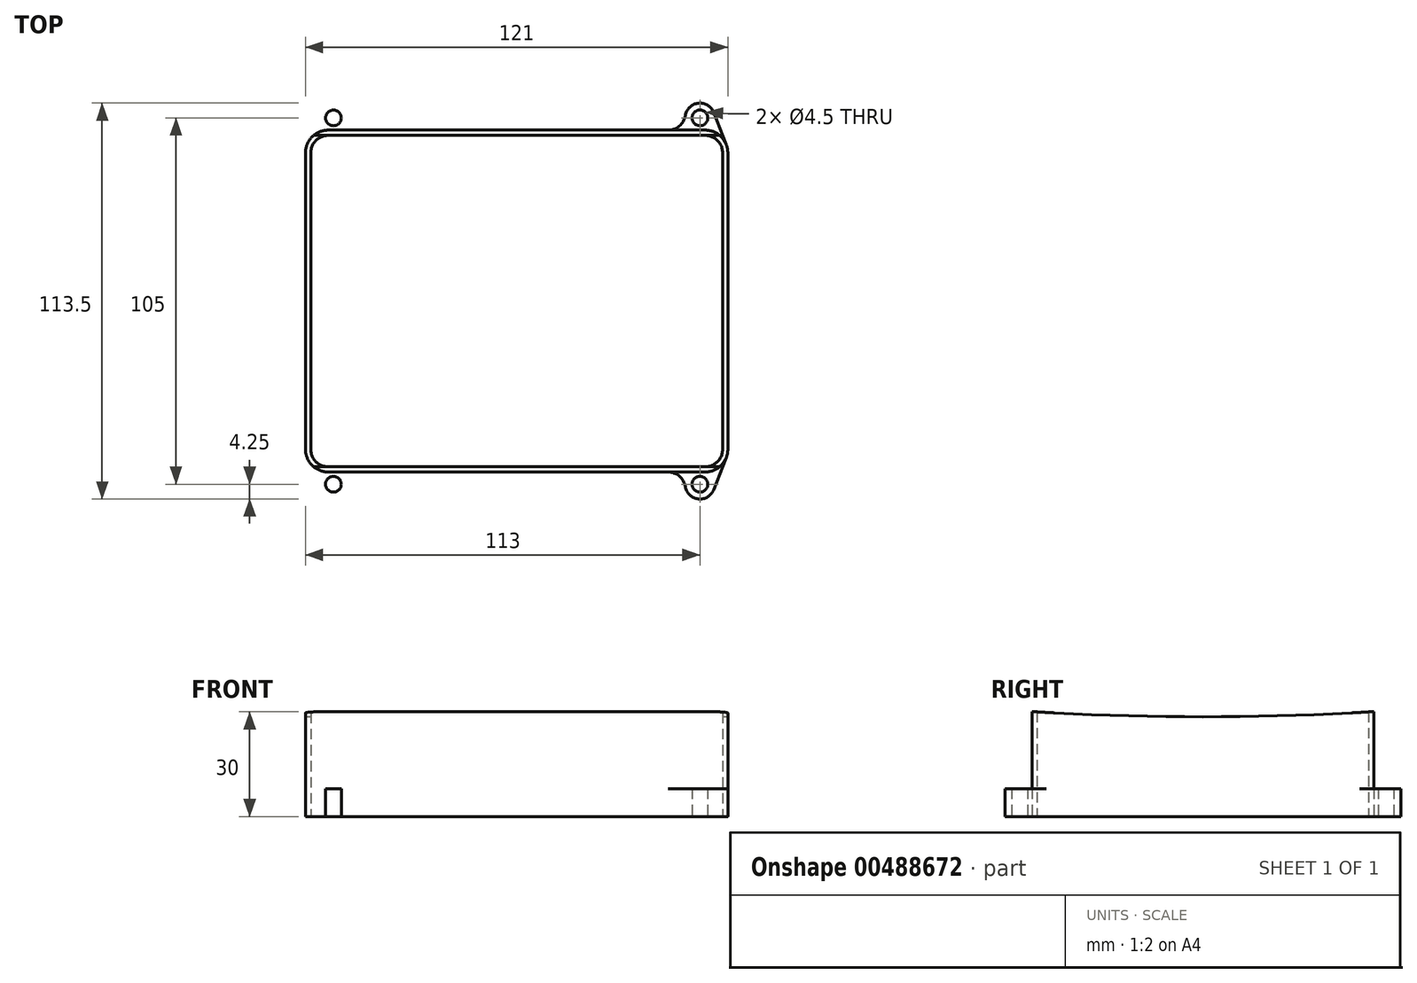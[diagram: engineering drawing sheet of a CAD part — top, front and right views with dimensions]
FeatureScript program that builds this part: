
annotation { "Feature Type Name" : "Feature", "Feature Type Description" : "" }
export const myFeature = defineFeature(function(context is Context, id is Id, definition is map)
    precondition{}
    {
        {
            var Q0;
            Q0=qCreatedBy(makeId("Top.planeOp"),FACE);
            var sketch = newSketch(context, id + "F0", { "sketchPlane" : qUnion([Q0])});
            skLineSegment(sketch, "E0.bottom", {"start": v(54, 47.5) * mm, "end": v(-54, 47.5) * mm});
            skLineSegment(sketch, "E0.top", {"start": v(54, -47.5) * mm, "end": v(-54, -47.5) * mm});
            skLineSegment(sketch, "E0.left", {"start": v(59, 42.5) * mm, "end": v(59, -42.5) * mm});
            skLineSegment(sketch, "E0.right", {"start": v(-59, 42.5) * mm, "end": v(-59, -42.5) * mm});
            skPoint(sketch, "E0.middle", {"position": v(0, 0) * mm});
            skLineSegment(sketch, "E1", {"start": v(0, 47.5) * mm, "end": v(0, -47.5) * mm, "construction": true});
            skCircle(sketch, "E2", {"center": v(52.5, -52.5) * mm, "radius": 2.25 * mm});
            skLineSegment(sketch, "E3", {"start": v(-59, 0) * mm, "end": v(59, 0) * mm, "construction": true});
            skCircle(sketch, "E4", {"center": v(52.5, 52.5) * mm, "radius": 2.25 * mm});
            skCircle(sketch, "E5.MirrorC", {"center": v(-52.5, 52.5) * mm, "radius": 2.25 * mm});
            skCircle(sketch, "E6.MirrorC", {"center": v(-52.5, -52.5) * mm, "radius": 2.25 * mm});
            skLineSegment(sketch, "E7", {"start": v(60.5, -42.5) * mm, "end": v(60.5, 42.5) * mm});
            skLineSegment(sketch, "E8.MirrorCS", {"start": v(-60.5, -42.5) * mm, "end": v(-60.5, 42.5) * mm});
            skLineSegment(sketch, "E9", {"start": v(-43.37, -49) * mm, "end": v(43.37, -49) * mm});
            skLineSegment(sketch, "E10.MirrorCS", {"start": v(-43.37, 49) * mm, "end": v(43.37, 49) * mm});
            skArc(sketch, "E11", {"start": v(48.3, -53.19) * mm, "mid": v(52.05, -56.73) * mm, "end": v(56.46, -54.05) * mm});
            skArc(sketch, "E12", {"start": v(48.3, -53.19) * mm, "mid": v(46.6, -50.19) * mm, "end": v(43.37, -49) * mm});
            skPoint(sketch, "E13.visualSharp", {"position": v(59, 47.5) * mm});
            skArc(sketch, "E13.filletArc", {"start": v(59, 42.5) * mm, "mid": v(57.54, 46.04) * mm, "end": v(54, 47.5) * mm});
            skPoint(sketch, "E14.visualSharp", {"position": v(59, -47.5) * mm});
            skArc(sketch, "E14.filletArc", {"start": v(54, -47.5) * mm, "mid": v(57.54, -46.04) * mm, "end": v(59, -42.5) * mm});
            skPoint(sketch, "E15.visualSharp", {"position": v(-59, -47.5) * mm});
            skArc(sketch, "E15.filletArc", {"start": v(-59, -42.5) * mm, "mid": v(-57.54, -46.04) * mm, "end": v(-54, -47.5) * mm});
            skPoint(sketch, "E16.visualSharp", {"position": v(-59, 47.5) * mm});
            skArc(sketch, "E16.filletArc", {"start": v(-54, 47.5) * mm, "mid": v(-57.54, 46.04) * mm, "end": v(-59, 42.5) * mm});
            skArc(sketch, "E17", {"start": v(60.05, -44.87) * mm, "mid": v(60.39, -43.7) * mm, "end": v(60.5, -42.5) * mm});
            skLineSegment(sketch, "E18", {"start": v(56.46, -54.05) * mm, "end": v(60.05, -44.87) * mm});
            skArc(sketch, "E19.MirrorCS", {"start": v(48.3, 53.19) * mm, "mid": v(46.6, 50.19) * mm, "end": v(43.37, 49) * mm});
            skArc(sketch, "E20.MirrorCS", {"start": v(48.3, 53.19) * mm, "mid": v(52.05, 56.73) * mm, "end": v(56.46, 54.05) * mm});
            skArc(sketch, "E21.MirrorCS", {"start": v(60.05, 44.87) * mm, "mid": v(60.39, 43.7) * mm, "end": v(60.5, 42.5) * mm});
            skLineSegment(sketch, "E22.MirrorCS", {"start": v(56.46, 54.05) * mm, "end": v(60.05, 44.87) * mm});
            skArc(sketch, "E23.MirrorCS", {"start": v(-60.05, 44.87) * mm, "mid": v(-60.39, 43.7) * mm, "end": v(-60.5, 42.5) * mm});
            skArc(sketch, "E24.MirrorCS", {"start": v(-60.05, -44.87) * mm, "mid": v(-60.39, -43.7) * mm, "end": v(-60.5, -42.5) * mm});
            skArc(sketch, "E25.MirrorCS", {"start": v(-48.3, -53.19) * mm, "mid": v(-46.6, -50.19) * mm, "end": v(-43.37, -49) * mm});
            skArc(sketch, "E26.MirrorCS", {"start": v(-48.3, -53.19) * mm, "mid": v(-52.05, -56.73) * mm, "end": v(-56.46, -54.05) * mm});
            skLineSegment(sketch, "E27.MirrorCS", {"start": v(-56.46, -54.05) * mm, "end": v(-60.05, -44.87) * mm});
            skLineSegment(sketch, "E28.MirrorCS", {"start": v(-56.46, 54.05) * mm, "end": v(-60.05, 44.87) * mm});
            skArc(sketch, "E29.MirrorCS", {"start": v(-48.3, 53.19) * mm, "mid": v(-52.05, 56.73) * mm, "end": v(-56.46, 54.05) * mm});
            skArc(sketch, "E30.MirrorCS", {"start": v(-48.3, 53.19) * mm, "mid": v(-46.6, 50.19) * mm, "end": v(-43.37, 49) * mm});
            skArc(sketch, "E31", {"start": v(-54, 49) * mm, "mid": v(-58.6, 47.1) * mm, "end": v(-60.5, 42.5) * mm});
            skLineSegment(sketch, "E32", {"start": v(-43.37, 49) * mm, "end": v(-54, 49) * mm});
            skLineSegment(sketch, "E33.MirrorCS", {"start": v(-43.37, -49) * mm, "end": v(-54, -49) * mm});
            skArc(sketch, "E34.MirrorCS", {"start": v(-54, -49) * mm, "mid": v(-58.6, -47.1) * mm, "end": v(-60.5, -42.5) * mm});
            skLineSegment(sketch, "E35.MirrorCS", {"start": v(43.37, 49) * mm, "end": v(54, 49) * mm});
            skArc(sketch, "E36.MirrorCS", {"start": v(54, 49) * mm, "mid": v(58.6, 47.1) * mm, "end": v(60.5, 42.5) * mm});
            skLineSegment(sketch, "E37.MirrorCS", {"start": v(43.37, -49) * mm, "end": v(54, -49) * mm});
            skArc(sketch, "E38.MirrorCS", {"start": v(54, -49) * mm, "mid": v(58.6, -47.1) * mm, "end": v(60.5, -42.5) * mm});
            skSolve(sketch);
        }
        {
            var Q0;
            Q0=makeQuery(id+"F0.imprint","IMPRINT",FACE,{"disambiguationData":[TD([[makeQuery(id+"F0.imprint","IMPRINT",EDGE,{"derivedFrom":sQuery(id+"F0.wireOp",EDGE,"E0.bottom")}),-1.0]])]});
            extrude(context, id + "F1", {"entities" : qUnion([Q0]), "depth" : 30 * mm});
        }
        {
            var Q0;
            Q0=makeQuery(id+"F0.imprint","IMPRINT",FACE,{"disambiguationData":[TD([[makeQuery(id+"F0.imprint","IMPRINT",EDGE,{"derivedFrom":sQuery(id+"F0.wireOp",EDGE,"E5.MirrorC")}),1.0]])]});
            var Q1;
            Q1=makeQuery(id+"F0.imprint","IMPRINT",FACE,{"disambiguationData":[TD([[makeQuery(id+"F0.imprint","IMPRINT",EDGE,{"derivedFrom":sQuery(id+"F0.wireOp",EDGE,"E6.MirrorC")}),1.0]])]});
            var Q2;
            Q2=makeQuery(id+"F0.imprint","IMPRINT",FACE,{"disambiguationData":[TD([[makeQuery(id+"F0.imprint","IMPRINT",EDGE,{"derivedFrom":sQuery(id+"F0.wireOp",EDGE,"E2")}),-1.0]])]});
            var Q3;
            Q3=makeQuery(id+"F0.imprint","IMPRINT",FACE,{"disambiguationData":[TD([[makeQuery(id+"F0.imprint","IMPRINT",EDGE,{"derivedFrom":sQuery(id+"F0.wireOp",EDGE,"E4")}),-1.0]])]});
            extrude(context, id + "F2", {"entities" : qUnion([Q0, Q1, Q2, Q3]), "operationType" : NewBodyOperationType.ADD, "depth" : 8 * mm});
        }
        {
            var Q0;
            Q0=makeQuery(id+"F1.opExtrude","SWEPT_FACE",FACE,{"disambiguationData":[OSD([sQuery(id+"F0.wireOp",EDGE,"E8.MirrorCS")])]});
            var sketch = newSketch(context, id + "F3", { "sketchPlane" : qUnion([Q0])});
            skCircle(sketch, "E39", {"center": v(0, 828.59) * mm, "radius": 800 * mm});
            skLineSegment(sketch, "E40", {"start": v(0, 30) * mm, "end": v(0, 828.59) * mm});
            skPoint(sketch, "E40.endSnap0", {"position": v(0, 30) * mm});
            skSolve(sketch);
        }
        {
            var Q0;
            Q0 = qSketchRegion(id + "F3", true);
            extrude(context, id + "F4", {"entities" : qUnion([Q0]), "operationType" : NewBodyOperationType.REMOVE, "endBound" : BoundingType.THROUGH_ALL, "oppositeDirection" : true, "depth" : 25 * mm});
        }
    });
